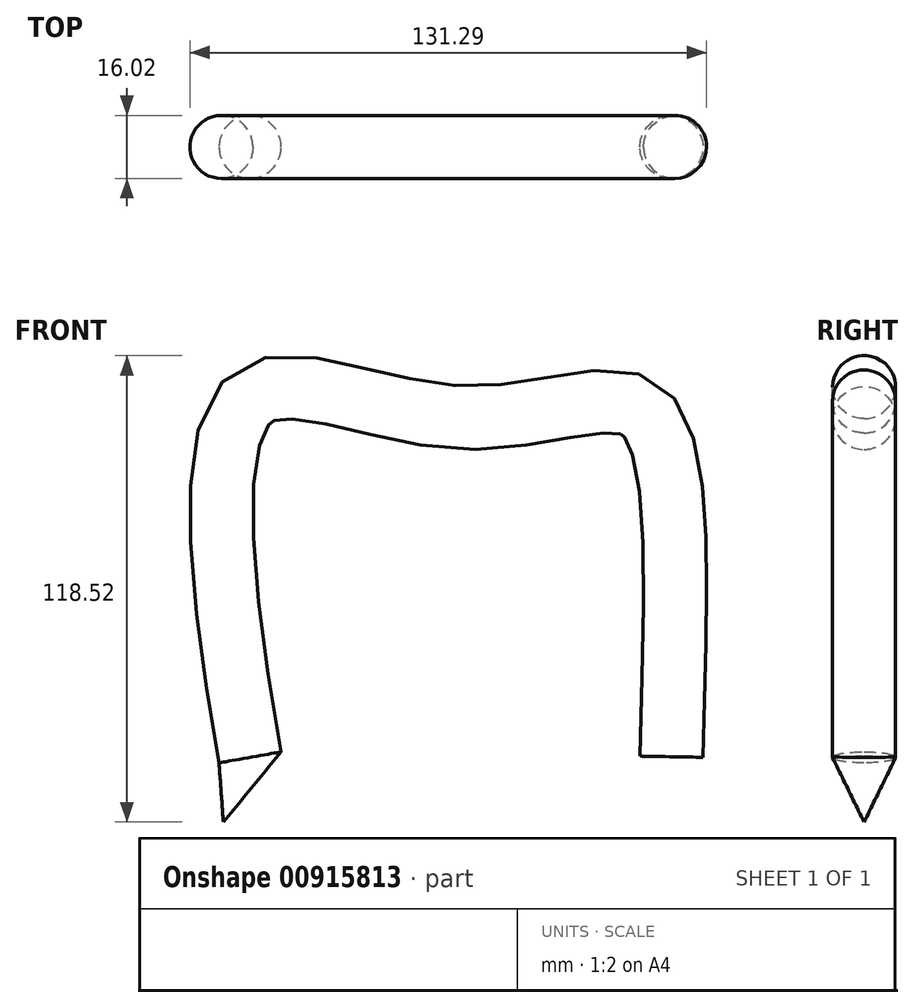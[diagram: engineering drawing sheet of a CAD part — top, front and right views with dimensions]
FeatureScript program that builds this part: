
annotation { "Feature Type Name" : "Feature", "Feature Type Description" : "" }
export const myFeature = defineFeature(function(context is Context, id is Id, definition is map)
    precondition{}
    {
        {
            var Q0;
            Q0=qCreatedBy(makeId("Front.planeOp"),FACE);
            var sketch = newSketch(context, id + "F0", { "sketchPlane" : qUnion([Q0])});
            skFitSpline(sketch, "E0", {"points": [v(-60.32, -42.95) * mm, v(-57.66, 51.53) * mm, v(-3.9, 45.68) * mm, v(41.52, 47.77) * mm, v(50.72, -42.47) * mm], "startDerivative": vector(-84.3, 471.58) * mm, "endDerivative": vector(-8.92, -471.16) * mm});
            skSolve(sketch);
        }
        {
            var Q0;
            Q0=sQuery(id+"F0.wireOp",VERTEX,"E0.start");
            var Q1;
            Q1=sQuery(id+"F0.wireOp",EDGE,"E0");
            cPlane(context, id + "F1", {"entities" : qUnion([Q0, Q1]), "cplaneType" : CPlaneType.CURVE_POINT, "offset" : 25.4 * mm, "width" : 152.4 * mm, "height" : 152.4 * mm});
        }
        {
            var Q0;
            Q0=qCreatedBy(id+"F1.planeOp",FACE);
            var sketch = newSketch(context, id + "F2", { "sketchPlane" : qUnion([Q0])});
            skCircle(sketch, "E1", {"center": v(-64.93, 0) * mm, "radius": 8 * mm});
            skSolve(sketch);
        }
        {
            var Q0;
            Q0=makeQuery(id+"F2.imprint","IMPRINT",FACE,{"disambiguationData":[TD([[makeQuery(id+"F2.imprint","IMPRINT",EDGE,{"derivedFrom":sQuery(id+"F2.wireOp",EDGE,"E1")}),1.0]])]});
            var Q1;
            Q1=sQuery(id+"F0.wireOp",EDGE,"E0");
            sweep(context, id + "F3", {"profiles" : qUnion([Q0]), "path" : qUnion([Q1])});
        }
        {
            var Q0;
            Q0=qCreatedBy(id+"F1.planeOp",FACE);
            cPlane(context, id + "F4", {"entities" : qUnion([Q0]), "cplaneType" : CPlaneType.OFFSET, "offset" : 15 * mm, "oppositeDirection" : true, "width" : 152.4 * mm, "height" : 152.4 * mm});
        }
        {
            var Q0;
            Q0=qCreatedBy(id+"F4.planeOp",FACE);
            var sketch = newSketch(context, id + "F5", { "sketchPlane" : qUnion([Q0])});
            skCircle(sketch, "E2", {"center": v(-74.5, 0) * mm, "radius": 1.88 * mm});
            skSolve(sketch);
        }
        {
            var Q1;
            Q1=sQuery(id+"F5.wireOp",VERTEX,"E2.center");
            var Q2;
            Q2 = qSketchRegion(id + "F2", true);
            loft(context, id + "F6", {"operationType" : NewBodyOperationType.ADD, "sheetProfilesArray" : [{ "sheetProfileEntities" : qUnion([Q1]) }, { "sheetProfileEntities" : qUnion([Q2]) }]});
        }
    });
